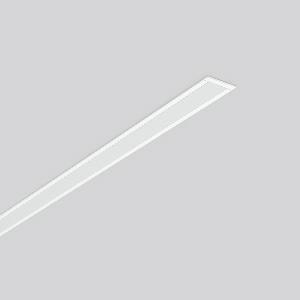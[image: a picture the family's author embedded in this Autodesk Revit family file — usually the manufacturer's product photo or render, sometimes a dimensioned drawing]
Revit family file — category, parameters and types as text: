
# Revit family: less_is_more_27_312178_002_1_76_c11b
name_source: partatom
category: Lighting Fixtures
units: mm (PartAtom-declared; Revit-internal decimal feet)

## family parameters
Cut with Voids When Loaded = No
Host = Face
Light Source = No
Part Type = Normal
Room Calculation Point = No
Round Connector Dimension = Use Diameter
Shared = No

## types (1)
- LESS IS MORE 27 (1 x LED Modul 840, 2900 lm, 4000)
    Apparent Load = 39 VA
    CIE Flux Codes = 48 79 96 100 100
    Color Rendering = 80
    Color Temperature = 4000
    Default Elevation = 1800 mm
    Description = Series: LESS IS MORE 27
Recessed ceiling and wall luminaire with slim design. Housing: extruded aluminium profile, powder-coated. End cap aluminium powder-coated. Diffuser made of non-yellowing plastic (PMMA), opal. Suitable for Recessed ceiling mounting, wall (recessed). External driver with connecting cable. 
Colour: traffic white, matt (RAL 9016)
Length: 1514 mm
Width: 38 mm
Height: 2 mm
Cut-out length: 1506 mm
Cut-out width: 30 mm
Recess height: 45-60 mm
Luminaire: recess height: 37 mm
Lamp: LED
Socket: without socket
Colour temperature: 4000K
Colour rendering index (CRI): 82
System power: 39 W
Rated luminous flux: 2900 lm
Beam angle Down: 110° / 114°
Luminous efficiency: 74 lm/W
Control gear: Voltage converter, DALI dim.
Protection class: II
Type of protection: IP 20
    Height = 0 mm  [stored 0 ft]
    Lamp = 1 x LED Modul 840
    Lamp Light Flux = 2900 lm
    Lamp count = 1
    Length = 1514 mm
    Lifetime = 50000 h
    Luminous efficacy = 74 lm/W
    Manufacturer = RZB
    ModVariant = No
    Model = 312178.002.1.76
    Mounting Place = Ceiling, Wall
    Mounting Type = Recessed
    Number of Poles = 1
    OnlyDefault = Yes
    Power Factor = 1
    Product Name = LESS IS MORE 27
    Product group = Recessed LED linear luminaires
    ProductGroupID = 407
    Protection Class = Protection class II
    Protection Degree = IP 20
    RLX_Detail_Level = 1
    RLX_Emergency_Light_Flux = 0 lm
    RLX_Emergency_Type = 0
    RLX_Emergency_Type_DB = No
    RlxData = <blob elided: 21617 chars, md5=f5e9657d>
    Socket = socket
    Standby Power = 0 W
    System Light Flux = 2900 lm
    System Power = 39 W
    Type Comments = ALEA SPOT
    Type Image = 312176.002.jpg
    URL = http://relux.com
    VarID = ---
    Voltage = 230 V
    Voltage Range = 220-240 V
    Weight = 0.00 kg
    Width = 38 mm

note: [stored X ft] marks values corroborated as IEEE doubles in the binary element streams (Revit-internal decimal feet)

## geometry (parser evidence)
native form markers: Blend x4, Sweep x11
no freeform markers — native parametric forms only
